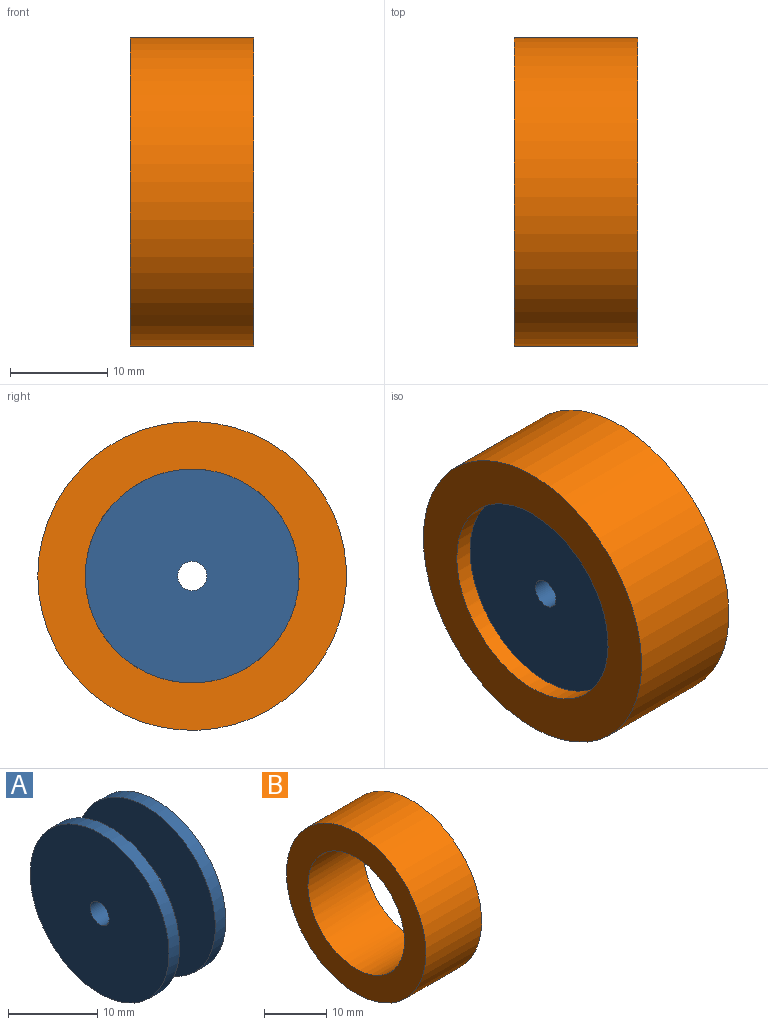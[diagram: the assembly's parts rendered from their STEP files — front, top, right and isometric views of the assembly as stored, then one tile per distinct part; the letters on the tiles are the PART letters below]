
ASSEMBLY  parts=2 mates=1
PART A: 8 faces, bbox 9x22x22 mm
  f0: cylinder r=11mm len=22mm, axis (-1,0,0), area 116.1mm2, adj f4,f7
  f1: cylinder r=1.5mm len=9mm, axis (-1,0,0), area 84.8mm2, adj f3,f4
  f2: cylinder r=11mm len=22mm, axis (-1,0,0), area 116.1mm2, adj f3,f6
  f3: plane 22x22mm, normal (1,0,0), area 373.1mm2, adj f1,f2
  f4: plane 22x22mm, normal (-1,0,0), area 373.1mm2, adj f0,f1
  f5: cylinder r=3.18mm len=6.36mm, axis (-1,0,0), area 112.7mm2, adj f6,f7
  f6: plane 22x22mm, normal (-1,0,0), area 348.4mm2, adj f2,f5
  f7: plane 22x22mm, normal (1,0,0), area 348.4mm2, adj f0,f5
PART B: 4 faces, bbox 12.7x31.8x31.8 mm
  f0: cylinder r=15.88mm len=31.75mm, axis (-1,0,0), area 1266.8mm2, adj f1,f2
  f1: plane 31.75x31.75mm, normal (1,0,0), area 411.6mm2, adj f0,f3
  f2: plane 31.75x31.75mm, normal (-1,0,0), area 411.6mm2, adj f0,f3
  f3: cylinder r=11mm len=22mm, axis (-1,0,0), area 877.8mm2, adj f1,f2
PLACE A t=(-4.93,30.07,-1.9)mm
PLACE B t=(-6.85,-5.98,0)mm
MATE fastened A.f0 <-> B.f0  axis (1,0,0) through (-3.25,25.15,61.79)mm
